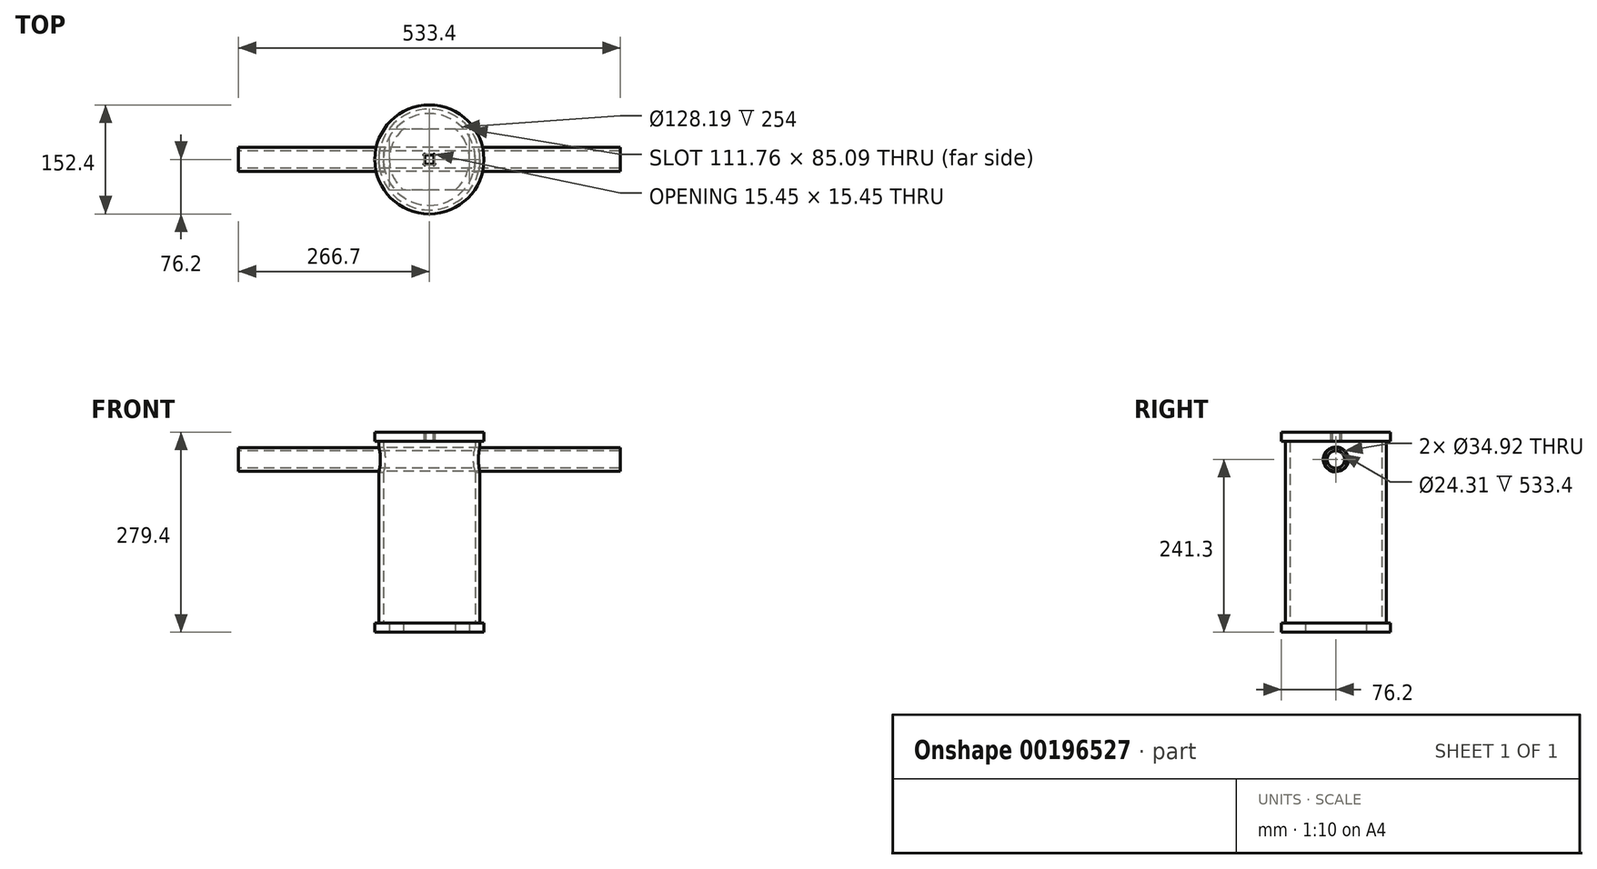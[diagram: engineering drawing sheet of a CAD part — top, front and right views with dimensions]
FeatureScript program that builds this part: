
annotation { "Feature Type Name" : "Feature", "Feature Type Description" : "" }
export const myFeature = defineFeature(function(context is Context, id is Id, definition is map)
    precondition{}
    {
        {
            var Q0;
            Q0=qCreatedBy(makeId("Top.planeOp"),FACE);
            var sketch = newSketch(context, id + "F0", { "sketchPlane" : qUnion([Q0])});
            skLineSegment(sketch, "E0.bottom", {"start": v(36.23, 42.55) * mm, "end": v(-36.23, 42.55) * mm});
            skLineSegment(sketch, "E0.top", {"start": v(36.23, -42.55) * mm, "end": v(-36.23, -42.55) * mm});
            skLineSegment(sketch, "E0.left", {"start": v(36.23, 42.55) * mm, "end": v(36.23, -42.54) * mm, "construction": true});
            skLineSegment(sketch, "E0.right", {"start": v(-36.23, 42.55) * mm, "end": v(-36.23, -42.55) * mm, "construction": true});
            skPoint(sketch, "E0.middle", {"position": v(0, 0) * mm});
            skLineSegment(sketch, "E1", {"start": v(0, 0) * mm, "end": v(0, 42.55) * mm, "construction": true});
            skArc(sketch, "E2", {"start": v(-36.23, 42.55) * mm, "mid": v(-55.88, 0) * mm, "end": v(-36.23, -42.55) * mm});
            skArc(sketch, "E3.MirrorCS", {"start": v(36.23, 42.55) * mm, "mid": v(55.88, 0) * mm, "end": v(36.23, -42.55) * mm});
            skCircle(sketch, "E4", {"center": v(0, 0) * mm, "radius": 76.2 * mm});
            skCircle(sketch, "E5", {"center": v(0, 0) * mm, "radius": 64.1 * mm, "construction": true});
            skSolve(sketch);
        }
        {
            var Q0;
            Q0 = qSketchRegion(id + "F0", true);
            extrude(context, id + "F1", {"entities" : qUnion([Q0]), "depth" : 12.7 * mm});
        }
        {
            var Q0;
            Q0=makeQuery(id+"F1.opExtrude","CAP_FACE",FACE,{"disambiguationData":[OSD([sQuery(id+"F0.wireOp",EDGE,"E0.bottom"),sQuery(id+"F0.wireOp",EDGE,"E0.top"),sQuery(id+"F0.wireOp",EDGE,"E2"),sQuery(id+"F0.wireOp",EDGE,"E3.MirrorCS"),sQuery(id+"F0.wireOp",EDGE,"E4")])],"isStart":false});
            var sketch = newSketch(context, id + "F2", { "sketchPlane" : qUnion([Q0])});
            skCircle(sketch, "E6", {"center": v(0, 0) * mm, "radius": 64.1 * mm});
            skCircle(sketch, "E7", {"center": v(0, 0) * mm, "radius": 70.65 * mm});
            skSolve(sketch);
        }
        {
            var Q0;
            Q0 = qSketchRegion(id + "F2", true);
            extrude(context, id + "F3", {"entities" : qUnion([Q0]), "operationType" : NewBodyOperationType.ADD, "offsetDistance" : 25.4 * mm, "depth" : 254 * mm});
        }
        {
            var Q0;
            Q0=makeQuery(id+"F3.opExtrude","CAP_FACE",FACE,{"disambiguationData":[OSD([sQuery(id+"F2.wireOp",EDGE,"E6"),sQuery(id+"F2.wireOp",EDGE,"E7")])],"isStart":false});
            var sketch = newSketch(context, id + "F4", { "sketchPlane" : qUnion([Q0])});
            skCircle(sketch, "E8.0", {"center": v(0, 0) * mm, "radius": 76.2 * mm});
            skLineSegment(sketch, "E9.bottom", {"start": v(5.2, 6.48) * mm, "end": v(-5.2, 6.48) * mm});
            skLineSegment(sketch, "E9.top", {"start": v(5.2, -6.48) * mm, "end": v(-5.2, -6.48) * mm});
            skLineSegment(sketch, "E9.left", {"start": v(6.48, 5.2) * mm, "end": v(6.48, -5.2) * mm});
            skLineSegment(sketch, "E9.right", {"start": v(-6.48, 5.2) * mm, "end": v(-6.48, -5.2) * mm});
            skArc(sketch, "E10", {"start": v(-5.2, 6.48) * mm, "mid": v(-7.38, 7.38) * mm, "end": v(-6.48, 5.2) * mm});
            skArc(sketch, "E11", {"start": v(6.48, 5.2) * mm, "mid": v(7.38, 7.38) * mm, "end": v(5.2, 6.48) * mm});
            skArc(sketch, "E12", {"start": v(-6.48, -5.2) * mm, "mid": v(-7.38, -7.38) * mm, "end": v(-5.2, -6.48) * mm});
            skArc(sketch, "E13", {"start": v(5.2, -6.48) * mm, "mid": v(7.38, -7.38) * mm, "end": v(6.48, -5.2) * mm});
            skLineSegment(sketch, "E14.bottom", {"start": v(6.35, 6.35) * mm, "end": v(-6.35, 6.35) * mm, "construction": true});
            skLineSegment(sketch, "E14.top", {"start": v(6.35, -6.35) * mm, "end": v(-6.35, -6.35) * mm, "construction": true});
            skLineSegment(sketch, "E14.left", {"start": v(6.35, 6.35) * mm, "end": v(6.35, -6.35) * mm, "construction": true});
            skLineSegment(sketch, "E14.right", {"start": v(-6.35, 6.35) * mm, "end": v(-6.35, -6.35) * mm, "construction": true});
            skSolve(sketch);
        }
        {
            var Q0;
            Q0 = qSketchRegion(id + "F4", true);
            extrude(context, id + "F5", {"entities" : qUnion([Q0]), "operationType" : NewBodyOperationType.ADD, "depth" : 12.7 * mm});
        }
        {
            var Q0;
            Q0=qCreatedBy(makeId("Right.planeOp"),FACE);
            var sketch = newSketch(context, id + "F6", { "sketchPlane" : qUnion([Q0])});
            skCircle(sketch, "E15", {"center": v(0, 241.3) * mm, "radius": 17.46 * mm});
            skSolve(sketch);
        }
        {
            var Q0;
            Q0 = qSketchRegion(id + "F6", true);
            extrude(context, id + "F7", {"entities" : qUnion([Q0]), "operationType" : NewBodyOperationType.REMOVE, "endBound" : BoundingType.THROUGH_ALL, "oppositeDirection" : true, "depth" : 25.4 * mm, "hasSecondDirection" : true, "secondDirectionBound" : SecondDirectionBoundingType.THROUGH_ALL, "secondDirectionOppositeDirection" : false, "secondDirectionDepth" : 25.4 * mm});
        }
        {
            var Q0;
            Q0=qCreatedBy(makeId("Right.planeOp"),FACE);
            var sketch = newSketch(context, id + "F8", { "sketchPlane" : qUnion([Q0])});
            skCircle(sketch, "E16", {"center": v(0, 241.3) * mm, "radius": 16.7 * mm});
            skCircle(sketch, "E17", {"center": v(0, 241.3) * mm, "radius": 12.15 * mm});
            skSolve(sketch);
        }
        {
            var Q0;
            Q0 = qSketchRegion(id + "F8", true);
            extrude(context, id + "F9", {"entities" : qUnion([Q0]), "endBound" : BoundingType.SYMMETRIC, "depth" : 533.4 * mm});
        }
    });
